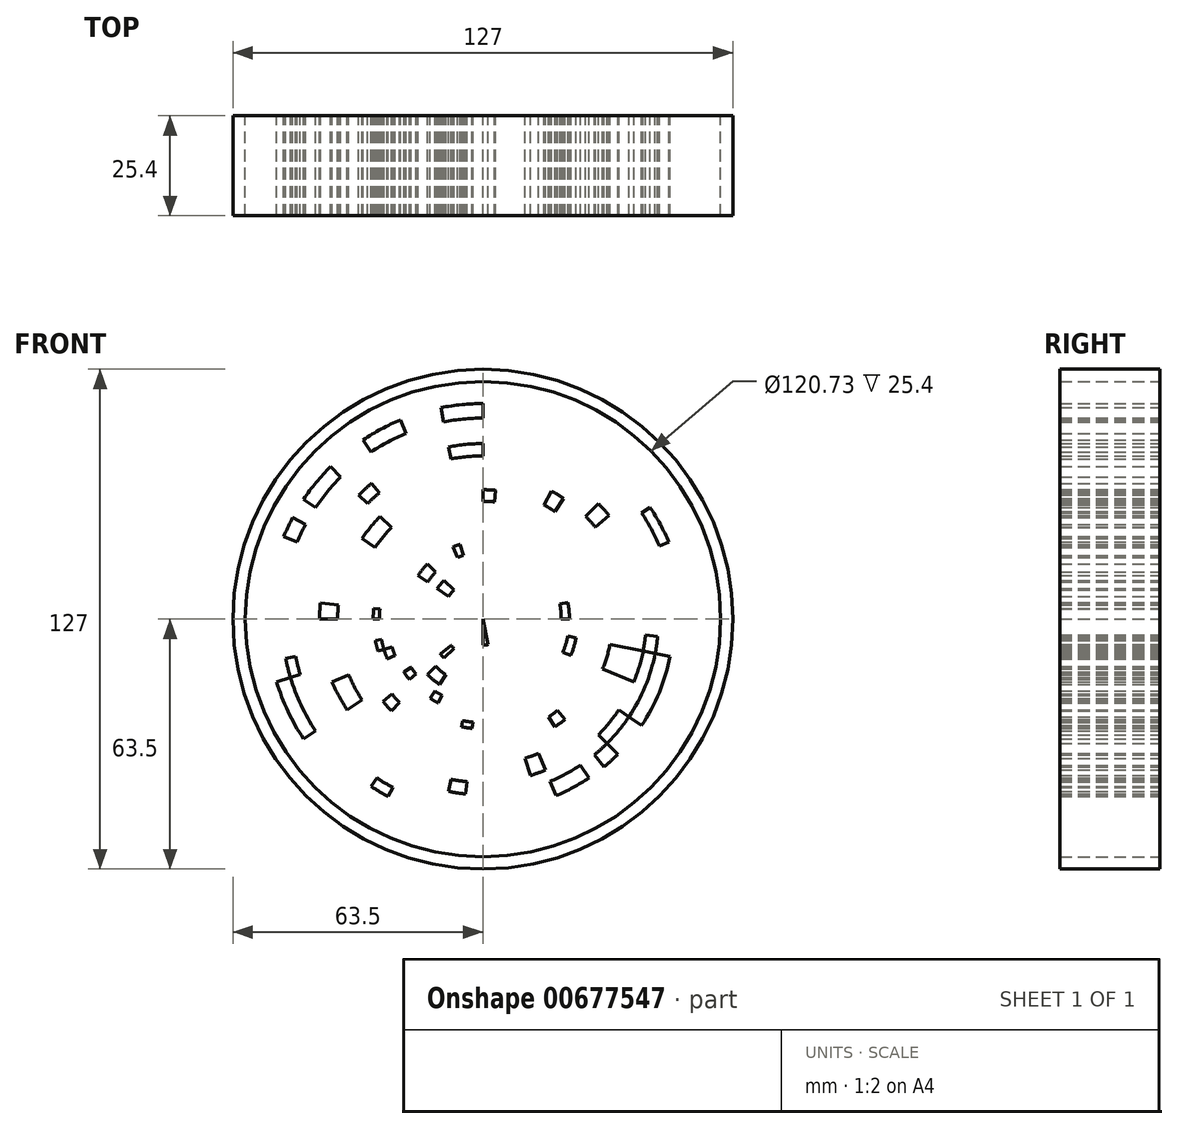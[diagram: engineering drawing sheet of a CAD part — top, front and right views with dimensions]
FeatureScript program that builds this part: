
annotation { "Feature Type Name" : "Feature", "Feature Type Description" : "" }
export const myFeature = defineFeature(function(context is Context, id is Id, definition is map)
    precondition{}
    {
        {
            var Q0;
            Q0=qCreatedBy(makeId("Front.planeOp"),FACE);
            var sketch = newSketch(context, id + "F0", { "sketchPlane" : qUnion([Q0])});
            skCircle(sketch, "E0", {"center": v(0, 0) * mm, "radius": 63.5 * mm});
            skCircle(sketch, "E1", {"center": v(0, 0) * mm, "radius": 6.6 * mm});
            skCircle(sketch, "E2", {"center": v(0, 0) * mm, "radius": 10.46 * mm});
            skCircle(sketch, "E3", {"center": v(0, 0) * mm, "radius": 13.98 * mm});
            skCircle(sketch, "E4", {"center": v(0, 0) * mm, "radius": 16.95 * mm});
            skCircle(sketch, "E5", {"center": v(0, 0) * mm, "radius": 19.9 * mm});
            skCircle(sketch, "E6", {"center": v(0, 0) * mm, "radius": 21.97 * mm});
            skCircle(sketch, "E7", {"center": v(0, 0) * mm, "radius": 24.15 * mm});
            skCircle(sketch, "E8", {"center": v(0, 0) * mm, "radius": 26.3 * mm});
            skCircle(sketch, "E9", {"center": v(0, 0) * mm, "radius": 27.88 * mm});
            skCircle(sketch, "E10", {"center": v(0, 0) * mm, "radius": 29.93 * mm});
            skCircle(sketch, "E11", {"center": v(0, 0) * mm, "radius": 32.9 * mm});
            skCircle(sketch, "E12", {"center": v(0, 0) * mm, "radius": 36.92 * mm});
            skCircle(sketch, "E13", {"center": v(0, 0) * mm, "radius": 41.5 * mm});
            skCircle(sketch, "E14", {"center": v(0, 0) * mm, "radius": 44.61 * mm});
            skCircle(sketch, "E15", {"center": v(0, 0) * mm, "radius": 48.5 * mm});
            skCircle(sketch, "E16", {"center": v(0, 0) * mm, "radius": 51.1 * mm});
            skCircle(sketch, "E17", {"center": v(0, 0) * mm, "radius": 54.79 * mm});
            skCircle(sketch, "E18", {"center": v(0, 0) * mm, "radius": 57 * mm});
            skCircle(sketch, "E19", {"center": v(0, 0) * mm, "radius": 60.37 * mm});
            skLineSegment(sketch, "E20", {"start": v(0, 0) * mm, "end": v(-44.9, 44.9) * mm});
            skLineSegment(sketch, "E21.1.0", {"start": v(0, 0) * mm, "end": v(-58.67, 24.3) * mm});
            skLineSegment(sketch, "E21.2.0", {"start": v(0, 0) * mm, "end": v(-63.5, 0) * mm});
            skLineSegment(sketch, "E21.3.0", {"start": v(0, 0) * mm, "end": v(-58.67, -24.3) * mm});
            skLineSegment(sketch, "E21.4.0", {"start": v(0, 0) * mm, "end": v(-44.9, -44.9) * mm});
            skLineSegment(sketch, "E21.5.0", {"start": v(0, 0) * mm, "end": v(-24.3, -58.67) * mm});
            skLineSegment(sketch, "E21.6.0", {"start": v(0, 0) * mm, "end": v(0, -63.5) * mm});
            skLineSegment(sketch, "E21.7.0", {"start": v(0, 0) * mm, "end": v(24.3, -58.67) * mm});
            skLineSegment(sketch, "E21.8.0", {"start": v(0, 0) * mm, "end": v(44.9, -44.9) * mm});
            skLineSegment(sketch, "E21.9.0", {"start": v(0, 0) * mm, "end": v(58.67, -24.3) * mm});
            skLineSegment(sketch, "E21.10.0", {"start": v(0, 0) * mm, "end": v(63.5, 0) * mm});
            skLineSegment(sketch, "E21.11.0", {"start": v(0, 0) * mm, "end": v(58.67, 24.3) * mm});
            skLineSegment(sketch, "E21.12.0", {"start": v(0, 0) * mm, "end": v(44.9, 44.9) * mm});
            skLineSegment(sketch, "E21.13.0", {"start": v(0, 0) * mm, "end": v(24.3, 58.67) * mm});
            skLineSegment(sketch, "E21.14.0", {"start": v(0, 0) * mm, "end": v(0, 63.5) * mm});
            skLineSegment(sketch, "E21.15.0", {"start": v(0, 0) * mm, "end": v(-24.3, 58.67) * mm});
            skLineSegment(sketch, "E22", {"start": v(0, 0) * mm, "end": v(-62.28, 12.39) * mm});
            skLineSegment(sketch, "E23.1.0", {"start": v(0, 0) * mm, "end": v(-62.28, -12.39) * mm});
            skLineSegment(sketch, "E23.2.0", {"start": v(0, 0) * mm, "end": v(-52.8, -35.28) * mm});
            skLineSegment(sketch, "E23.3.0", {"start": v(0, 0) * mm, "end": v(-35.28, -52.8) * mm});
            skLineSegment(sketch, "E23.4.0", {"start": v(0, 0) * mm, "end": v(-12.39, -62.28) * mm});
            skLineSegment(sketch, "E23.5.0", {"start": v(0, 0) * mm, "end": v(12.39, -62.28) * mm});
            skLineSegment(sketch, "E23.6.0", {"start": v(0, 0) * mm, "end": v(35.28, -52.8) * mm});
            skLineSegment(sketch, "E23.7.0", {"start": v(0, 0) * mm, "end": v(52.8, -35.28) * mm});
            skLineSegment(sketch, "E23.8.0", {"start": v(0, 0) * mm, "end": v(62.28, -12.39) * mm});
            skLineSegment(sketch, "E23.9.0", {"start": v(0, 0) * mm, "end": v(62.28, 12.39) * mm});
            skLineSegment(sketch, "E23.10.0", {"start": v(0, 0) * mm, "end": v(52.8, 35.28) * mm});
            skLineSegment(sketch, "E23.11.0", {"start": v(0, 0) * mm, "end": v(35.28, 52.8) * mm});
            skLineSegment(sketch, "E23.12.0", {"start": v(0, 0) * mm, "end": v(12.39, 62.28) * mm});
            skLineSegment(sketch, "E23.13.0", {"start": v(0, 0) * mm, "end": v(-12.39, 62.28) * mm});
            skLineSegment(sketch, "E23.14.0", {"start": v(0, 0) * mm, "end": v(-35.28, 52.8) * mm});
            skLineSegment(sketch, "E23.15.0", {"start": v(0, 0) * mm, "end": v(-52.8, 35.28) * mm});
            skLineSegment(sketch, "E24", {"start": v(-63.2, 6.22) * mm, "end": v(0, 0) * mm});
            skLineSegment(sketch, "E25.1.0", {"start": v(-60.77, -18.43) * mm, "end": v(0, 0) * mm});
            skLineSegment(sketch, "E25.2.0", {"start": v(-49.09, -40.28) * mm, "end": v(0, 0) * mm});
            skLineSegment(sketch, "E25.3.0", {"start": v(-29.93, -56) * mm, "end": v(0, 0) * mm});
            skLineSegment(sketch, "E25.4.0", {"start": v(-6.22, -63.2) * mm, "end": v(0, 0) * mm});
            skLineSegment(sketch, "E25.5.0", {"start": v(18.43, -60.77) * mm, "end": v(0, 0) * mm});
            skLineSegment(sketch, "E25.6.0", {"start": v(40.28, -49.09) * mm, "end": v(0, 0) * mm});
            skLineSegment(sketch, "E25.7.0", {"start": v(56, -29.93) * mm, "end": v(0, 0) * mm});
            skLineSegment(sketch, "E25.8.0", {"start": v(63.2, -6.22) * mm, "end": v(0, 0) * mm});
            skLineSegment(sketch, "E25.9.0", {"start": v(60.77, 18.43) * mm, "end": v(0, 0) * mm});
            skLineSegment(sketch, "E25.10.0", {"start": v(49.09, 40.28) * mm, "end": v(0, 0) * mm});
            skLineSegment(sketch, "E25.11.0", {"start": v(29.93, 56) * mm, "end": v(0, 0) * mm});
            skLineSegment(sketch, "E25.12.0", {"start": v(6.22, 63.2) * mm, "end": v(0, 0) * mm});
            skLineSegment(sketch, "E25.13.0", {"start": v(-18.43, 60.77) * mm, "end": v(0, 0) * mm});
            skLineSegment(sketch, "E25.14.0", {"start": v(-40.28, 49.09) * mm, "end": v(0, 0) * mm});
            skLineSegment(sketch, "E25.15.0", {"start": v(-56, 29.93) * mm, "end": v(0, 0) * mm});
            skSolve(sketch);
        }
        {
            var Q0;
            Q0 = qSketchRegion(id + "F0", true);
            var Q1;
            {var subQ0=sQuery(id+"F0.wireOp",EDGE,"E23.3.0");var subQ1=sQuery(id+"F0.wireOp",EDGE,"E6");var subQ2=makeQuery(id+"F0.imprint","INTERSECT",VERTEX,{"derivedFrom":[subQ1,subQ0]});Q1=makeQuery(id+"F0.imprint","IMPRINT",FACE,{"disambiguationData":[TD([[makeQuery(id+"F0.imprint","IMPRINT",EDGE,{"disambiguationData":[TD([[subQ2,-1.0]])],"derivedFrom":subQ1}),-1.0]])]});}
            var Q2;
            {var subQ0=sQuery(id+"F0.wireOp",EDGE,"E23.4.0");var subQ1=sQuery(id+"F0.wireOp",EDGE,"E8");var subQ2=makeQuery(id+"F0.imprint","INTERSECT",VERTEX,{"derivedFrom":[subQ1,subQ0]});Q2=makeQuery(id+"F0.imprint","IMPRINT",FACE,{"disambiguationData":[TD([[makeQuery(id+"F0.imprint","IMPRINT",EDGE,{"disambiguationData":[TD([[subQ2,-1.0]])],"derivedFrom":subQ1}),-1.0]])]});}
            var Q3;
            {var subQ0=sQuery(id+"F0.wireOp",EDGE,"E25.5.0");var subQ1=sQuery(id+"F0.wireOp",EDGE,"E12");var subQ2=makeQuery(id+"F0.imprint","INTERSECT",VERTEX,{"derivedFrom":[subQ1,subQ0]});Q3=makeQuery(id+"F0.imprint","IMPRINT",FACE,{"disambiguationData":[TD([[makeQuery(id+"F0.imprint","IMPRINT",EDGE,{"disambiguationData":[TD([[subQ2,-1.0]])],"derivedFrom":subQ1}),-1.0]])]});}
            var Q4;
            {var subQ0=sQuery(id+"F0.wireOp",EDGE,"E23.9.0");var subQ1=sQuery(id+"F0.wireOp",EDGE,"E5");var subQ2=makeQuery(id+"F0.imprint","INTERSECT",VERTEX,{"derivedFrom":[subQ1,subQ0]});Q4=makeQuery(id+"F0.imprint","IMPRINT",FACE,{"disambiguationData":[TD([[makeQuery(id+"F0.imprint","IMPRINT",EDGE,{"disambiguationData":[TD([[subQ2,1.0]])],"derivedFrom":subQ1}),-1.0]])]});}
            var Q5;
            {var subQ0=sQuery(id+"F0.wireOp",EDGE,"E25.13.0");var subQ1=sQuery(id+"F0.wireOp",EDGE,"E4");var subQ2=makeQuery(id+"F0.imprint","INTERSECT",VERTEX,{"derivedFrom":[subQ1,subQ0]});Q5=makeQuery(id+"F0.imprint","IMPRINT",FACE,{"disambiguationData":[TD([[makeQuery(id+"F0.imprint","IMPRINT",EDGE,{"disambiguationData":[TD([[subQ2,-1.0]])],"derivedFrom":subQ1}),-1.0]])]});}
            var Q6;
            {var subQ0=sQuery(id+"F0.wireOp",EDGE,"E20");var subQ1=sQuery(id+"F0.wireOp",EDGE,"E4");var subQ2=makeQuery(id+"F0.imprint","INTERSECT",VERTEX,{"derivedFrom":[subQ1,subQ0]});Q6=makeQuery(id+"F0.imprint","IMPRINT",FACE,{"disambiguationData":[TD([[makeQuery(id+"F0.imprint","IMPRINT",EDGE,{"disambiguationData":[TD([[subQ2,-1.0]])],"derivedFrom":subQ1}),-1.0]])]});}
            var Q7;
            {var subQ0=sQuery(id+"F0.wireOp",EDGE,"E20");var subQ1=sQuery(id+"F0.wireOp",EDGE,"E2");var subQ2=makeQuery(id+"F0.imprint","INTERSECT",VERTEX,{"derivedFrom":[subQ1,subQ0]});Q7=makeQuery(id+"F0.imprint","IMPRINT",FACE,{"disambiguationData":[TD([[makeQuery(id+"F0.imprint","IMPRINT",EDGE,{"disambiguationData":[TD([[subQ2,-1.0]])],"derivedFrom":subQ1}),-1.0]])]});}
            var Q8;
            {var subQ0=sQuery(id+"F0.wireOp",EDGE,"E24");var subQ1=sQuery(id+"F0.wireOp",EDGE,"E8");var subQ2=makeQuery(id+"F0.imprint","INTERSECT",VERTEX,{"derivedFrom":[subQ1,subQ0]});Q8=makeQuery(id+"F0.imprint","IMPRINT",FACE,{"disambiguationData":[TD([[makeQuery(id+"F0.imprint","IMPRINT",EDGE,{"disambiguationData":[TD([[subQ2,-1.0]])],"derivedFrom":subQ1}),-1.0]])]});}
            var Q9;
            {var subQ0=sQuery(id+"F0.wireOp",EDGE,"E23.6.0");var subQ1=sQuery(id+"F0.wireOp",EDGE,"E10");var subQ2=makeQuery(id+"F0.imprint","INTERSECT",VERTEX,{"derivedFrom":[subQ1,subQ0]});Q9=makeQuery(id+"F0.imprint","IMPRINT",FACE,{"disambiguationData":[TD([[makeQuery(id+"F0.imprint","IMPRINT",EDGE,{"disambiguationData":[TD([[subQ2,-1.0]])],"derivedFrom":subQ1}),-1.0]])]});}
            var Q10;
            {var subQ0=sQuery(id+"F0.wireOp",EDGE,"E25.5.0");var subQ1=sQuery(id+"F0.wireOp",EDGE,"E12");var subQ2=makeQuery(id+"F0.imprint","INTERSECT",VERTEX,{"derivedFrom":[subQ1,subQ0]});Q10=makeQuery(id+"F0.imprint","IMPRINT",FACE,{"disambiguationData":[TD([[makeQuery(id+"F0.imprint","IMPRINT",EDGE,{"disambiguationData":[TD([[subQ2,-1.0]])],"derivedFrom":subQ1}),-1.0]])]});}
            var Q11;
            {var subQ0=sQuery(id+"F0.wireOp",EDGE,"E23.4.0");var subQ1=sQuery(id+"F0.wireOp",EDGE,"E13");var subQ2=makeQuery(id+"F0.imprint","INTERSECT",VERTEX,{"derivedFrom":[subQ1,subQ0]});Q11=makeQuery(id+"F0.imprint","IMPRINT",FACE,{"disambiguationData":[TD([[makeQuery(id+"F0.imprint","IMPRINT",EDGE,{"disambiguationData":[TD([[subQ2,-1.0]])],"derivedFrom":subQ1}),-1.0]])]});}
            var Q12;
            {var subQ0=sQuery(id+"F0.wireOp",EDGE,"E23.3.0");var subQ1=sQuery(id+"F0.wireOp",EDGE,"E15");var subQ2=makeQuery(id+"F0.imprint","INTERSECT",VERTEX,{"derivedFrom":[subQ1,subQ0]});Q12=makeQuery(id+"F0.imprint","IMPRINT",FACE,{"disambiguationData":[TD([[makeQuery(id+"F0.imprint","IMPRINT",EDGE,{"disambiguationData":[TD([[subQ2,-1.0]])],"derivedFrom":subQ1}),-1.0]])]});}
            var Q13;
            {var subQ0=sQuery(id+"F0.wireOp",EDGE,"E21.3.0");var subQ1=sQuery(id+"F0.wireOp",EDGE,"E16");var subQ2=makeQuery(id+"F0.imprint","INTERSECT",VERTEX,{"derivedFrom":[subQ1,subQ0]});Q13=makeQuery(id+"F0.imprint","IMPRINT",FACE,{"disambiguationData":[TD([[makeQuery(id+"F0.imprint","IMPRINT",EDGE,{"disambiguationData":[TD([[subQ2,-1.0]])],"derivedFrom":subQ1}),-1.0]])]});}
            var Q14;
            {var subQ0=sQuery(id+"F0.wireOp",EDGE,"E25.1.0");var subQ1=sQuery(id+"F0.wireOp",EDGE,"E16");var subQ2=makeQuery(id+"F0.imprint","INTERSECT",VERTEX,{"derivedFrom":[subQ1,subQ0]});Q14=makeQuery(id+"F0.imprint","IMPRINT",FACE,{"disambiguationData":[TD([[makeQuery(id+"F0.imprint","IMPRINT",EDGE,{"disambiguationData":[TD([[subQ2,-1.0]])],"derivedFrom":subQ1}),-1.0]])]});}
            var Q15;
            {var subQ0=sQuery(id+"F0.wireOp",EDGE,"E23.1.0");var subQ1=sQuery(id+"F0.wireOp",EDGE,"E15");var subQ2=makeQuery(id+"F0.imprint","INTERSECT",VERTEX,{"derivedFrom":[subQ1,subQ0]});Q15=makeQuery(id+"F0.imprint","IMPRINT",FACE,{"disambiguationData":[TD([[makeQuery(id+"F0.imprint","IMPRINT",EDGE,{"disambiguationData":[TD([[subQ2,-1.0]])],"derivedFrom":subQ1}),-1.0]])]});}
            var Q16;
            {var subQ0=sQuery(id+"F0.wireOp",EDGE,"E21.9.0");var subQ1=sQuery(id+"F0.wireOp",EDGE,"E11");var subQ2=makeQuery(id+"F0.imprint","INTERSECT",VERTEX,{"derivedFrom":[subQ1,subQ0]});Q16=makeQuery(id+"F0.imprint","IMPRINT",FACE,{"disambiguationData":[TD([[makeQuery(id+"F0.imprint","IMPRINT",EDGE,{"disambiguationData":[TD([[subQ2,-1.0]])],"derivedFrom":subQ1}),-1.0]])]});}
            var Q17;
            {var subQ0=sQuery(id+"F0.wireOp",EDGE,"E21.9.0");var subQ1=sQuery(id+"F0.wireOp",EDGE,"E12");var subQ2=makeQuery(id+"F0.imprint","INTERSECT",VERTEX,{"derivedFrom":[subQ1,subQ0]});Q17=makeQuery(id+"F0.imprint","IMPRINT",FACE,{"disambiguationData":[TD([[makeQuery(id+"F0.imprint","IMPRINT",EDGE,{"disambiguationData":[TD([[subQ2,-1.0]])],"derivedFrom":subQ1}),-1.0]])]});}
            var Q18;
            {var subQ0=sQuery(id+"F0.wireOp",EDGE,"E21.9.0");var subQ1=sQuery(id+"F0.wireOp",EDGE,"E14");var subQ2=makeQuery(id+"F0.imprint","INTERSECT",VERTEX,{"derivedFrom":[subQ1,subQ0]});Q18=makeQuery(id+"F0.imprint","IMPRINT",FACE,{"disambiguationData":[TD([[makeQuery(id+"F0.imprint","IMPRINT",EDGE,{"disambiguationData":[TD([[subQ2,-1.0]])],"derivedFrom":subQ1}),-1.0]])]});}
            var Q19;
            {var subQ0=sQuery(id+"F0.wireOp",EDGE,"E25.7.0");var subQ1=sQuery(id+"F0.wireOp",EDGE,"E14");var subQ2=makeQuery(id+"F0.imprint","INTERSECT",VERTEX,{"derivedFrom":[subQ1,subQ0]});Q19=makeQuery(id+"F0.imprint","IMPRINT",FACE,{"disambiguationData":[TD([[makeQuery(id+"F0.imprint","IMPRINT",EDGE,{"disambiguationData":[TD([[subQ2,-1.0]])],"derivedFrom":subQ1}),-1.0]])]});}
            var Q20;
            {var subQ0=sQuery(id+"F0.wireOp",EDGE,"E23.7.0");var subQ1=sQuery(id+"F0.wireOp",EDGE,"E14");var subQ2=makeQuery(id+"F0.imprint","INTERSECT",VERTEX,{"derivedFrom":[subQ1,subQ0]});Q20=makeQuery(id+"F0.imprint","IMPRINT",FACE,{"disambiguationData":[TD([[makeQuery(id+"F0.imprint","IMPRINT",EDGE,{"disambiguationData":[TD([[subQ2,-1.0]])],"derivedFrom":subQ1}),-1.0]])]});}
            var Q21;
            {var subQ0=sQuery(id+"F0.wireOp",EDGE,"E21.8.0");var subQ1=sQuery(id+"F0.wireOp",EDGE,"E13");var subQ2=makeQuery(id+"F0.imprint","INTERSECT",VERTEX,{"derivedFrom":[subQ1,subQ0]});Q21=makeQuery(id+"F0.imprint","IMPRINT",FACE,{"disambiguationData":[TD([[makeQuery(id+"F0.imprint","IMPRINT",EDGE,{"disambiguationData":[TD([[subQ2,-1.0]])],"derivedFrom":subQ1}),-1.0]])]});}
            var Q22;
            {var subQ0=sQuery(id+"F0.wireOp",EDGE,"E25.6.0");var subQ1=sQuery(id+"F0.wireOp",EDGE,"E14");var subQ2=makeQuery(id+"F0.imprint","INTERSECT",VERTEX,{"derivedFrom":[subQ1,subQ0]});Q22=makeQuery(id+"F0.imprint","IMPRINT",FACE,{"disambiguationData":[TD([[makeQuery(id+"F0.imprint","IMPRINT",EDGE,{"disambiguationData":[TD([[subQ2,-1.0]])],"derivedFrom":subQ1}),-1.0]])]});}
            var Q23;
            {var subQ0=sQuery(id+"F0.wireOp",EDGE,"E21.7.0");var subQ1=sQuery(id+"F0.wireOp",EDGE,"E14");var subQ2=makeQuery(id+"F0.imprint","INTERSECT",VERTEX,{"derivedFrom":[subQ1,subQ0]});Q23=makeQuery(id+"F0.imprint","IMPRINT",FACE,{"disambiguationData":[TD([[makeQuery(id+"F0.imprint","IMPRINT",EDGE,{"disambiguationData":[TD([[subQ2,-1.0]])],"derivedFrom":subQ1}),-1.0]])]});}
            var Q24;
            {var subQ0=sQuery(id+"F0.wireOp",EDGE,"E21.6.0");var subQ1=sQuery(id+"F0.wireOp",EDGE,"E1");var subQ2=makeQuery(id+"F0.imprint","INTERSECT",VERTEX,{"derivedFrom":[subQ1,subQ0]});Q24=makeQuery(id+"F0.imprint","IMPRINT",FACE,{"disambiguationData":[TD([[makeQuery(id+"F0.imprint","IMPRINT",EDGE,{"disambiguationData":[TD([[subQ2,-1.0]])],"derivedFrom":subQ1}),1.0]])]});}
            var Q25;
            {var subQ0=sQuery(id+"F0.wireOp",EDGE,"E21.14.0");var subQ1=sQuery(id+"F0.wireOp",EDGE,"E13");var subQ2=makeQuery(id+"F0.imprint","INTERSECT",VERTEX,{"derivedFrom":[subQ1,subQ0]});Q25=makeQuery(id+"F0.imprint","IMPRINT",FACE,{"disambiguationData":[TD([[makeQuery(id+"F0.imprint","IMPRINT",EDGE,{"disambiguationData":[TD([[subQ2,-1.0]])],"derivedFrom":subQ1}),-1.0]])]});}
            var Q26;
            {var subQ0=sQuery(id+"F0.wireOp",EDGE,"E25.14.0");var subQ1=sQuery(id+"F0.wireOp",EDGE,"E13");var subQ2=makeQuery(id+"F0.imprint","INTERSECT",VERTEX,{"derivedFrom":[subQ1,subQ0]});Q26=makeQuery(id+"F0.imprint","IMPRINT",FACE,{"disambiguationData":[TD([[makeQuery(id+"F0.imprint","IMPRINT",EDGE,{"disambiguationData":[TD([[subQ2,-1.0]])],"derivedFrom":subQ1}),-1.0]])]});}
            var Q27;
            {var subQ0=sQuery(id+"F0.wireOp",EDGE,"E25.2.0");var subQ1=sQuery(id+"F0.wireOp",EDGE,"E2");var subQ2=makeQuery(id+"F0.imprint","INTERSECT",VERTEX,{"derivedFrom":[subQ1,subQ0]});Q27=makeQuery(id+"F0.imprint","IMPRINT",FACE,{"disambiguationData":[TD([[makeQuery(id+"F0.imprint","IMPRINT",EDGE,{"disambiguationData":[TD([[subQ2,-1.0]])],"derivedFrom":subQ1}),-1.0]])]});}
            var Q28;
            {var subQ0=sQuery(id+"F0.wireOp",EDGE,"E23.1.0");var subQ1=sQuery(id+"F0.wireOp",EDGE,"E8");var subQ2=makeQuery(id+"F0.imprint","INTERSECT",VERTEX,{"derivedFrom":[subQ1,subQ0]});Q28=makeQuery(id+"F0.imprint","IMPRINT",FACE,{"disambiguationData":[TD([[makeQuery(id+"F0.imprint","IMPRINT",EDGE,{"disambiguationData":[TD([[subQ2,-1.0]])],"derivedFrom":subQ1}),-1.0]])]});}
            var Q29;
            {var subQ0=sQuery(id+"F0.wireOp",EDGE,"E21.3.0");var subQ1=sQuery(id+"F0.wireOp",EDGE,"E12");var subQ2=makeQuery(id+"F0.imprint","INTERSECT",VERTEX,{"derivedFrom":[subQ1,subQ0]});Q29=makeQuery(id+"F0.imprint","IMPRINT",FACE,{"disambiguationData":[TD([[makeQuery(id+"F0.imprint","IMPRINT",EDGE,{"disambiguationData":[TD([[subQ2,-1.0]])],"derivedFrom":subQ1}),-1.0]])]});}
            var Q30;
            {var subQ0=sQuery(id+"F0.wireOp",EDGE,"E25.2.0");var subQ1=sQuery(id+"F0.wireOp",EDGE,"E10");var subQ2=makeQuery(id+"F0.imprint","INTERSECT",VERTEX,{"derivedFrom":[subQ1,subQ0]});Q30=makeQuery(id+"F0.imprint","IMPRINT",FACE,{"disambiguationData":[TD([[makeQuery(id+"F0.imprint","IMPRINT",EDGE,{"disambiguationData":[TD([[subQ2,-1.0]])],"derivedFrom":subQ1}),-1.0]])]});}
            var Q31;
            {var subQ0=sQuery(id+"F0.wireOp",EDGE,"E23.2.0");var subQ1=sQuery(id+"F0.wireOp",EDGE,"E6");var subQ2=makeQuery(id+"F0.imprint","INTERSECT",VERTEX,{"derivedFrom":[subQ1,subQ0]});Q31=makeQuery(id+"F0.imprint","IMPRINT",FACE,{"disambiguationData":[TD([[makeQuery(id+"F0.imprint","IMPRINT",EDGE,{"disambiguationData":[TD([[subQ2,-1.0]])],"derivedFrom":subQ1}),-1.0]])]});}
            var Q32;
            {var subQ0=sQuery(id+"F0.wireOp",EDGE,"E25.12.0");var subQ1=sQuery(id+"F0.wireOp",EDGE,"E10");var subQ2=makeQuery(id+"F0.imprint","INTERSECT",VERTEX,{"derivedFrom":[subQ1,subQ0]});Q32=makeQuery(id+"F0.imprint","IMPRINT",FACE,{"disambiguationData":[TD([[makeQuery(id+"F0.imprint","IMPRINT",EDGE,{"disambiguationData":[TD([[subQ2,-1.0]])],"derivedFrom":subQ1}),-1.0]])]});}
            var Q33;
            {var subQ0=sQuery(id+"F0.wireOp",EDGE,"E20");var subQ1=sQuery(id+"F0.wireOp",EDGE,"E11");var subQ2=makeQuery(id+"F0.imprint","INTERSECT",VERTEX,{"derivedFrom":[subQ1,subQ0]});Q33=makeQuery(id+"F0.imprint","IMPRINT",FACE,{"disambiguationData":[TD([[makeQuery(id+"F0.imprint","IMPRINT",EDGE,{"disambiguationData":[TD([[subQ2,-1.0]])],"derivedFrom":subQ1}),-1.0]])]});}
            var Q34;
            {var subQ0=sQuery(id+"F0.wireOp",EDGE,"E25.1.0");var subQ1=sQuery(id+"F0.wireOp",EDGE,"E7");var subQ2=makeQuery(id+"F0.imprint","INTERSECT",VERTEX,{"derivedFrom":[subQ1,subQ0]});Q34=makeQuery(id+"F0.imprint","IMPRINT",FACE,{"disambiguationData":[TD([[makeQuery(id+"F0.imprint","IMPRINT",EDGE,{"disambiguationData":[TD([[subQ2,-1.0]])],"derivedFrom":subQ1}),-1.0]])]});}
            var Q35;
            {var subQ0=sQuery(id+"F0.wireOp",EDGE,"E21.9.0");var subQ1=sQuery(id+"F0.wireOp",EDGE,"E6");var subQ2=makeQuery(id+"F0.imprint","INTERSECT",VERTEX,{"derivedFrom":[subQ1,subQ0]});Q35=makeQuery(id+"F0.imprint","IMPRINT",FACE,{"disambiguationData":[TD([[makeQuery(id+"F0.imprint","IMPRINT",EDGE,{"disambiguationData":[TD([[subQ2,-1.0]])],"derivedFrom":subQ1}),-1.0]])]});}
            var Q36;
            {var subQ0=sQuery(id+"F0.wireOp",EDGE,"E25.10.0");var subQ1=sQuery(id+"F0.wireOp",EDGE,"E12");var subQ2=makeQuery(id+"F0.imprint","INTERSECT",VERTEX,{"derivedFrom":[subQ1,subQ0]});Q36=makeQuery(id+"F0.imprint","IMPRINT",FACE,{"disambiguationData":[TD([[makeQuery(id+"F0.imprint","IMPRINT",EDGE,{"disambiguationData":[TD([[subQ2,-1.0]])],"derivedFrom":subQ1}),-1.0]])]});}
            var Q37;
            {var subQ0=sQuery(id+"F0.wireOp",EDGE,"E23.11.0");var subQ1=sQuery(id+"F0.wireOp",EDGE,"E11");var subQ2=makeQuery(id+"F0.imprint","INTERSECT",VERTEX,{"derivedFrom":[subQ1,subQ0]});Q37=makeQuery(id+"F0.imprint","IMPRINT",FACE,{"disambiguationData":[TD([[makeQuery(id+"F0.imprint","IMPRINT",EDGE,{"disambiguationData":[TD([[subQ2,-1.0]])],"derivedFrom":subQ1}),-1.0]])]});}
            var Q38;
            {var subQ0=sQuery(id+"F0.wireOp",EDGE,"E21.14.0");var subQ1=sQuery(id+"F0.wireOp",EDGE,"E16");var subQ2=makeQuery(id+"F0.imprint","INTERSECT",VERTEX,{"derivedFrom":[subQ1,subQ0]});Q38=makeQuery(id+"F0.imprint","IMPRINT",FACE,{"disambiguationData":[TD([[makeQuery(id+"F0.imprint","IMPRINT",EDGE,{"disambiguationData":[TD([[subQ2,-1.0]])],"derivedFrom":subQ1}),-1.0]])]});}
            var Q39;
            {var subQ0=sQuery(id+"F0.wireOp",EDGE,"E21.15.0");var subQ1=sQuery(id+"F0.wireOp",EDGE,"E16");var subQ2=makeQuery(id+"F0.imprint","INTERSECT",VERTEX,{"derivedFrom":[subQ1,subQ0]});Q39=makeQuery(id+"F0.imprint","IMPRINT",FACE,{"disambiguationData":[TD([[makeQuery(id+"F0.imprint","IMPRINT",EDGE,{"disambiguationData":[TD([[subQ2,-1.0]])],"derivedFrom":subQ1}),-1.0]])]});}
            var Q40;
            {var subQ0=sQuery(id+"F0.wireOp",EDGE,"E20");var subQ1=sQuery(id+"F0.wireOp",EDGE,"E16");var subQ2=makeQuery(id+"F0.imprint","INTERSECT",VERTEX,{"derivedFrom":[subQ1,subQ0]});Q40=makeQuery(id+"F0.imprint","IMPRINT",FACE,{"disambiguationData":[TD([[makeQuery(id+"F0.imprint","IMPRINT",EDGE,{"disambiguationData":[TD([[subQ2,-1.0]])],"derivedFrom":subQ1}),-1.0]])]});}
            var Q41;
            {var subQ0=sQuery(id+"F0.wireOp",EDGE,"E25.15.0");var subQ1=sQuery(id+"F0.wireOp",EDGE,"E16");var subQ2=makeQuery(id+"F0.imprint","INTERSECT",VERTEX,{"derivedFrom":[subQ1,subQ0]});Q41=makeQuery(id+"F0.imprint","IMPRINT",FACE,{"disambiguationData":[TD([[makeQuery(id+"F0.imprint","IMPRINT",EDGE,{"disambiguationData":[TD([[subQ2,-1.0]])],"derivedFrom":subQ1}),-1.0]])]});}
            var Q42;
            {var subQ0=sQuery(id+"F0.wireOp",EDGE,"E24");var subQ1=sQuery(id+"F0.wireOp",EDGE,"E12");var subQ2=makeQuery(id+"F0.imprint","INTERSECT",VERTEX,{"derivedFrom":[subQ1,subQ0]});Q42=makeQuery(id+"F0.imprint","IMPRINT",FACE,{"disambiguationData":[TD([[makeQuery(id+"F0.imprint","IMPRINT",EDGE,{"disambiguationData":[TD([[subQ2,-1.0]])],"derivedFrom":subQ1}),-1.0]])]});}
            var Q43;
            {var subQ0=sQuery(id+"F0.wireOp",EDGE,"E21.4.0");var subQ1=sQuery(id+"F0.wireOp",EDGE,"E4");var subQ2=makeQuery(id+"F0.imprint","INTERSECT",VERTEX,{"derivedFrom":[subQ1,subQ0]});Q43=makeQuery(id+"F0.imprint","IMPRINT",FACE,{"disambiguationData":[TD([[makeQuery(id+"F0.imprint","IMPRINT",EDGE,{"disambiguationData":[TD([[subQ2,-1.0]])],"derivedFrom":subQ1}),-1.0]])]});}
            var Q44;
            {var subQ0=sQuery(id+"F0.wireOp",EDGE,"E23.8.0");var subQ1=sQuery(id+"F0.wireOp",EDGE,"E13");var subQ2=makeQuery(id+"F0.imprint","INTERSECT",VERTEX,{"derivedFrom":[subQ1,subQ0]});Q44=makeQuery(id+"F0.imprint","IMPRINT",FACE,{"disambiguationData":[TD([[makeQuery(id+"F0.imprint","IMPRINT",EDGE,{"disambiguationData":[TD([[subQ2,-1.0]])],"derivedFrom":subQ1}),-1.0]])]});}
            var Q45;
            {var subQ0=sQuery(id+"F0.wireOp",EDGE,"E21.11.0");var subQ1=sQuery(id+"F0.wireOp",EDGE,"E15");var subQ2=makeQuery(id+"F0.imprint","INTERSECT",VERTEX,{"derivedFrom":[subQ1,subQ0]});Q45=makeQuery(id+"F0.imprint","IMPRINT",FACE,{"disambiguationData":[TD([[makeQuery(id+"F0.imprint","IMPRINT",EDGE,{"disambiguationData":[TD([[subQ2,-1.0]])],"derivedFrom":subQ1}),-1.0]])]});}
            extrude(context, id + "F1", {"entities" : qUnion([Q0, Q1, Q2, Q3, Q4, Q5, Q6, Q7, Q8, Q9, Q10, Q11, Q12, Q13, Q14, Q15, Q16, Q17, Q18, Q19, Q20, Q21, Q22, Q23, Q24, Q25, Q26, Q27, Q28, Q29, Q30, Q31, Q32, Q33, Q34, Q35, Q36, Q37, Q38, Q39, Q40, Q41, Q42, Q43, Q44, Q45]), "depth" : 25.4 * mm, "offsetDistance" : 25.4 * mm});
        }
    });
